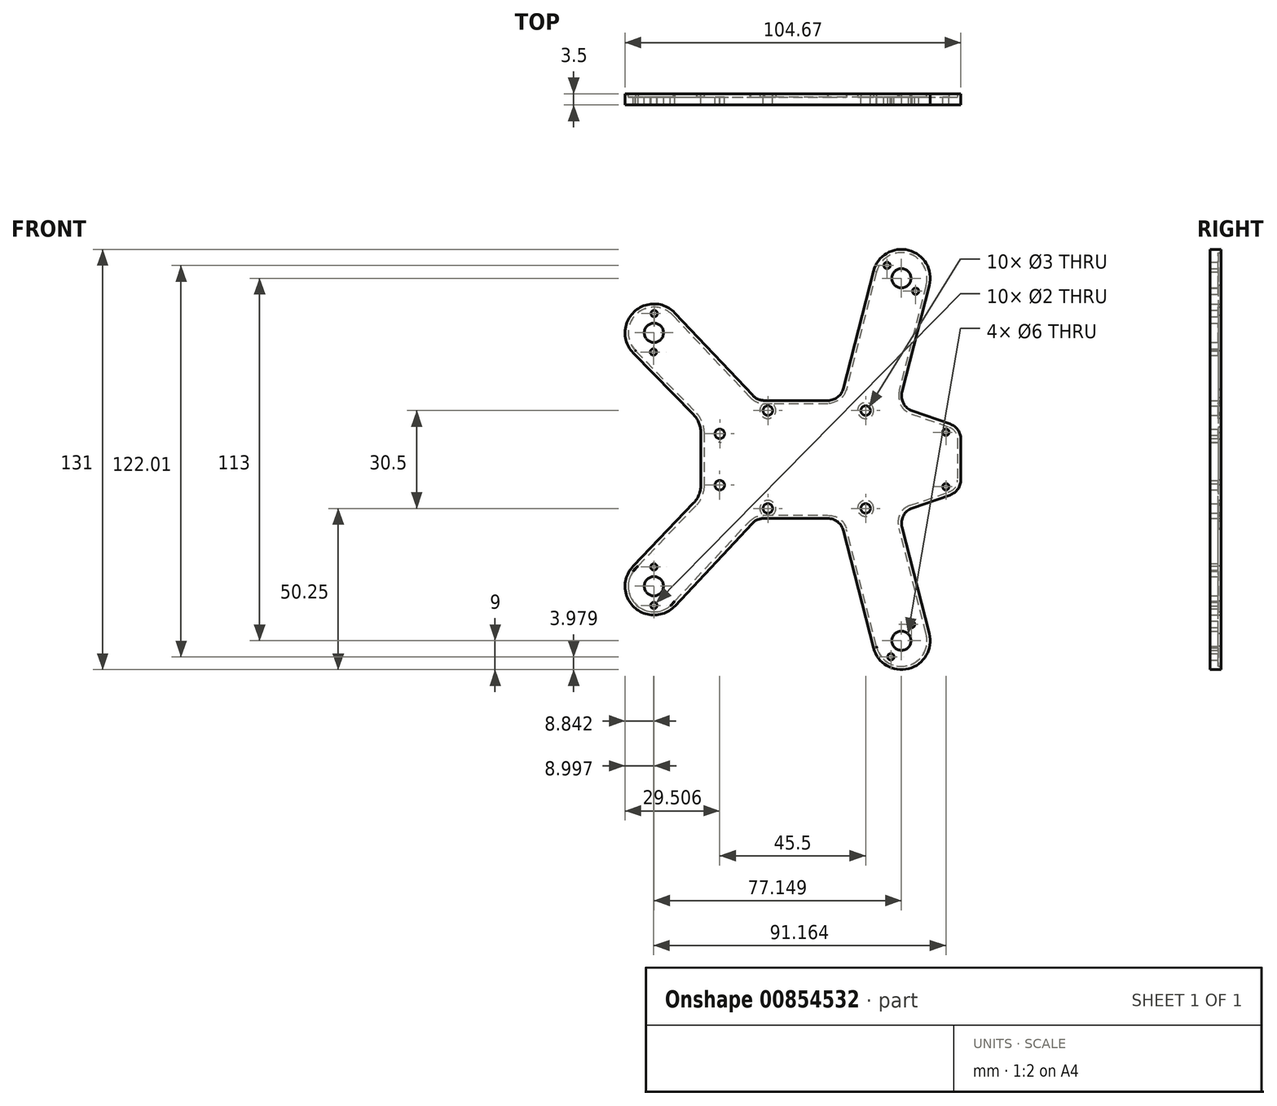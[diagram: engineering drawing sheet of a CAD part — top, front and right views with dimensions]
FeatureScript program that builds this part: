
annotation { "Feature Type Name" : "Feature", "Feature Type Description" : "" }
export const myFeature = defineFeature(function(context is Context, id is Id, definition is map)
    precondition{}
    {
        {
            var Q0;
            Q0=qCreatedBy(makeId("Front.planeOp"),FACE);
            var sketch = newSketch(context, id + "F0", { "sketchPlane" : qUnion([Q0])});
            skLineSegment(sketch, "E0.bottom", {"start": v(-3.88, -18.39) * mm, "end": v(-23.86, -18.39) * mm});
            skLineSegment(sketch, "E0.top", {"start": v(-3.88, 18.39) * mm, "end": v(-23.64, 18.39) * mm});
            skLineSegment(sketch, "E0.left", {"start": v(37.58, -6.33) * mm, "end": v(37.58, -5.89) * mm});
            skLineSegment(sketch, "E0.right", {"start": v(-37.58, -5.3) * mm, "end": v(-37.58, 5.3) * mm});
            skPoint(sketch, "E0.middle", {"position": v(0, 0) * mm});
            skPoint(sketch, "E1", {"position": v(-22.58, 15.25) * mm});
            skPoint(sketch, "E2", {"position": v(-22.58, -15.25) * mm});
            skPoint(sketch, "E3", {"position": v(7.92, 15.25) * mm});
            skPoint(sketch, "E4", {"position": v(7.92, -15.25) * mm});
            skPoint(sketch, "E5", {"position": v(32.92, 8.5) * mm});
            skPoint(sketch, "E6", {"position": v(32.92, -8.5) * mm});
            skCircle(sketch, "E7", {"center": v(-22.58, 15.25) * mm, "radius": 1.5 * mm});
            skCircle(sketch, "E8", {"center": v(-22.58, -15.25) * mm, "radius": 1.5 * mm});
            skCircle(sketch, "E9", {"center": v(7.92, 15.25) * mm, "radius": 1.5 * mm});
            skCircle(sketch, "E10", {"center": v(7.92, -15.25) * mm, "radius": 1.5 * mm});
            skCircle(sketch, "E11", {"center": v(32.92, 8.5) * mm, "radius": 1 * mm});
            skCircle(sketch, "E12", {"center": v(32.92, -8.5) * mm, "radius": 1 * mm});
            skArc(sketch, "E13", {"start": v(-37.47, 5.41) * mm, "mid": v(-37.53, 5.35) * mm, "end": v(-37.58, 5.3) * mm});
            skLineSegment(sketch, "E14", {"start": v(-37.47, 5.41) * mm, "end": v(-37.58, 5.3) * mm});
            skPoint(sketch, "E15.orphan", {"position": v(-37.58, 18.39) * mm});
            skPoint(sketch, "E16.orphan", {"position": v(-37.58, -18.39) * mm});
            skPoint(sketch, "E17", {"position": v(37.58, -9.89) * mm});
            skPoint(sketch, "E18", {"position": v(37.58, 9.89) * mm});
            skLineSegment(sketch, "E19", {"start": v(22.48, 15.14) * mm, "end": v(34.23, 11.05) * mm});
            skLineSegment(sketch, "E20", {"start": v(22.48, -15.14) * mm, "end": v(34.23, -11.05) * mm});
            skPoint(sketch, "E21.orphan", {"position": v(37.58, 18.39) * mm});
            skPoint(sketch, "E22.orphan", {"position": v(37.58, -18.39) * mm});
            skPoint(sketch, "E23", {"position": v(37.58, 5.89) * mm});
            skPoint(sketch, "E24", {"position": v(37.58, -5.89) * mm});
            skLineSegment(sketch, "E25.trimOffspring", {"start": v(37.58, 5.89) * mm, "end": v(37.58, 6.33) * mm});
            skPoint(sketch, "E26", {"position": v(-58.1, 39.5) * mm});
            skPoint(sketch, "E27", {"position": v(-58.1, -39.5) * mm});
            skPoint(sketch, "E28", {"position": v(19.06, -56.5) * mm});
            skPoint(sketch, "E29", {"position": v(19.06, 56.5) * mm});
            skPoint(sketch, "E30.center.orphan", {"position": v(-19.86, 0) * mm});
            skPoint(sketch, "E31.center.orphan", {"position": v(23.9, 0) * mm});
            skLineSegment(sketch, "E32", {"start": v(37.58, 5.89) * mm, "end": v(37.58, -5.89) * mm});
            skCircle(sketch, "E33", {"center": v(-58.1, -39.5) * mm, "radius": 3 * mm});
            skCircle(sketch, "E34", {"center": v(-58.1, 39.5) * mm, "radius": 3 * mm});
            skCircle(sketch, "E35", {"center": v(19.06, 56.5) * mm, "radius": 3 * mm});
            skCircle(sketch, "E36", {"center": v(19.06, -56.5) * mm, "radius": 3 * mm});
            skArc(sketch, "E37", {"start": v(-64.59, -33.27) * mm, "mid": v(-64.28, -46.03) * mm, "end": v(-51.52, -45.65) * mm});
            skArc(sketch, "E38", {"start": v(10.34, -58.73) * mm, "mid": v(21.29, -65.22) * mm, "end": v(27.77, -54.27) * mm});
            skArc(sketch, "E39", {"start": v(-51.55, 45.68) * mm, "mid": v(-64.33, 46) * mm, "end": v(-64.53, 33.21) * mm});
            skArc(sketch, "E40", {"start": v(27.77, 54.27) * mm, "mid": v(21.29, 65.22) * mm, "end": v(10.34, 58.73) * mm});
            skLineSegment(sketch, "E41", {"start": v(-45.75, 13.98) * mm, "end": v(-64.53, 33.21) * mm});
            skLineSegment(sketch, "E42", {"start": v(-27.27, 19.96) * mm, "end": v(-51.55, 45.68) * mm});
            skLineSegment(sketch, "E43", {"start": v(-27.52, -19.97) * mm, "end": v(-51.52, -45.65) * mm});
            skLineSegment(sketch, "E44", {"start": v(-45.7, -13.58) * mm, "end": v(-64.59, -33.27) * mm});
            skLineSegment(sketch, "E45", {"start": v(27.77, 54.27) * mm, "end": v(19.28, 21.1) * mm});
            skLineSegment(sketch, "E46", {"start": v(19.28, -21.1) * mm, "end": v(27.77, -54.27) * mm});
            skLineSegment(sketch, "E47", {"start": v(0.96, -22.15) * mm, "end": v(10.34, -58.73) * mm});
            skLineSegment(sketch, "E48", {"start": v(0.96, 22.15) * mm, "end": v(10.34, 58.73) * mm});
            skLineSegment(sketch, "E49", {"start": v(-43.47, 8.4) * mm, "end": v(-43.47, -8.04) * mm});
            skPoint(sketch, "E50.newPointA", {"position": v(13.14, -18.39) * mm});
            skPoint(sketch, "E50.newPointB", {"position": v(0, -18.39) * mm});
            skArc(sketch, "E50.filletArc", {"start": v(0.96, -22.15) * mm, "mid": v(-0.81, -19.44) * mm, "end": v(-3.88, -18.39) * mm});
            skPoint(sketch, "E51.newPointA", {"position": v(0, 18.39) * mm});
            skPoint(sketch, "E51.newPointB", {"position": v(13.14, 18.39) * mm});
            skArc(sketch, "E51.filletArc", {"start": v(-3.88, 18.39) * mm, "mid": v(-0.81, 19.44) * mm, "end": v(0.96, 22.15) * mm});
            skPoint(sketch, "E52.visualSharp", {"position": v(-25.8, 18.39) * mm});
            skArc(sketch, "E52.filletArc", {"start": v(-27.27, 19.96) * mm, "mid": v(-25.62, 18.8) * mm, "end": v(-23.64, 18.39) * mm});
            skPoint(sketch, "E53.visualSharp", {"position": v(-26.03, -18.39) * mm});
            skArc(sketch, "E53.filletArc", {"start": v(-23.86, -18.39) * mm, "mid": v(-25.85, -18.8) * mm, "end": v(-27.52, -19.97) * mm});
            skArc(sketch, "E54.filletArc", {"start": v(-45.7, -13.58) * mm, "mid": v(-44.05, -11.02) * mm, "end": v(-43.47, -8.04) * mm});
            skArc(sketch, "E55.filletArc", {"start": v(-43.47, 8.4) * mm, "mid": v(-44.06, 11.41) * mm, "end": v(-45.75, 13.98) * mm});
            skPoint(sketch, "E56.newPointA", {"position": v(18.14, 16.65) * mm});
            skArc(sketch, "E56.filletArc", {"start": v(19.28, 21.1) * mm, "mid": v(19.72, 17.5) * mm, "end": v(22.48, 15.14) * mm});
            skPoint(sketch, "E57.newPointB", {"position": v(18.14, -16.65) * mm});
            skArc(sketch, "E57.filletArc", {"start": v(22.48, -15.14) * mm, "mid": v(19.72, -17.5) * mm, "end": v(19.28, -21.1) * mm});
            skArc(sketch, "E58.filletArc", {"start": v(34.23, -11.05) * mm, "mid": v(36.66, -9.23) * mm, "end": v(37.58, -6.33) * mm});
            skArc(sketch, "E59.filletArc", {"start": v(37.58, 6.33) * mm, "mid": v(36.66, 9.23) * mm, "end": v(34.23, 11.05) * mm});
            skLineSegment(sketch, "E60", {"start": v(-37.56, 8) * mm, "end": v(-37.56, 0) * mm});
            skLineSegment(sketch, "E61", {"start": v(-37.56, 0) * mm, "end": v(-37.58, -8) * mm});
            skCircle(sketch, "E62", {"center": v(-37.56, 8) * mm, "radius": 1.5 * mm});
            skCircle(sketch, "E63", {"center": v(-37.58, -8) * mm, "radius": 1.5 * mm});
            skCircle(sketch, "E64", {"center": v(-58.02, 45.5) * mm, "radius": 1 * mm});
            skCircle(sketch, "E65", {"center": v(-58.25, 33.5) * mm, "radius": 1 * mm});
            skCircle(sketch, "E66", {"center": v(-58.1, -33.5) * mm, "radius": 1 * mm});
            skCircle(sketch, "E67", {"center": v(-58.1, -45.5) * mm, "radius": 1 * mm});
            skCircle(sketch, "E68", {"center": v(14.57, 60.49) * mm, "radius": 1 * mm});
            skCircle(sketch, "E69", {"center": v(23.49, 52.46) * mm, "radius": 1 * mm});
            skCircle(sketch, "E70", {"center": v(15.77, -61.52) * mm, "radius": 1 * mm});
            skCircle(sketch, "E71", {"center": v(22.24, -51.42) * mm, "radius": 1 * mm});
            skArc(sketch, "E72", {"start": v(-63.03, -33.2) * mm, "mid": v(-63.64, -45.26) * mm, "end": v(-51.62, -44.2) * mm});
            skLineSegment(sketch, "E73", {"start": v(-64.59, -34.83) * mm, "end": v(-44.8, -14.2) * mm});
            skLineSegment(sketch, "E74", {"start": v(-52.97, -45.65) * mm, "end": v(-28.27, -19.22) * mm});
            skLineSegment(sketch, "E75", {"start": v(-23.86, -17.39) * mm, "end": v(-3.93, -17.39) * mm});
            skArc(sketch, "E76", {"start": v(11.25, -58.24) * mm, "mid": v(21.04, -64.25) * mm, "end": v(26.74, -54.27) * mm});
            skLineSegment(sketch, "E77", {"start": v(11.37, -58.73) * mm, "end": v(1.9, -21.79) * mm});
            skLineSegment(sketch, "E78", {"start": v(26.74, -54.27) * mm, "end": v(18.34, -21.5) * mm});
            skLineSegment(sketch, "E79", {"start": v(21.69, -14.35) * mm, "end": v(33.57, -10.22) * mm});
            skLineSegment(sketch, "E80", {"start": v(36.58, 6.32) * mm, "end": v(36.58, -6.4) * mm});
            skLineSegment(sketch, "E81", {"start": v(22.13, 14.2) * mm, "end": v(33.89, 10.11) * mm});
            skArc(sketch, "E82", {"start": v(26.74, 54.27) * mm, "mid": v(21.14, 64.22) * mm, "end": v(11.3, 58.44) * mm});
            skLineSegment(sketch, "E83", {"start": v(26.74, 54.27) * mm, "end": v(18.38, 21.64) * mm});
            skLineSegment(sketch, "E84", {"start": v(11.32, 58.53) * mm, "end": v(1.93, 21.88) * mm});
            skLineSegment(sketch, "E85", {"start": v(-3.8, 17.39) * mm, "end": v(-23.64, 17.39) * mm});
            skArc(sketch, "E86", {"start": v(-52.15, 44.86) * mm, "mid": v(-63.6, 45.3) * mm, "end": v(-63.75, 33.84) * mm});
            skLineSegment(sketch, "E87", {"start": v(-52.15, 44.86) * mm, "end": v(-28.01, 19.28) * mm});
            skLineSegment(sketch, "E88", {"start": v(-63.88, 33.98) * mm, "end": v(-44.93, 14.58) * mm});
            skLineSegment(sketch, "E89", {"start": v(-42.47, 8.37) * mm, "end": v(-42.47, -7.92) * mm});
            skFitSpline(sketch, "E90", {"points": [v(-44.93, 14.58) * mm, v(-43.18, 11.84) * mm, v(-42.47, 8.37) * mm], "startDerivative": vector(4.86, -5.6) * mm, "endDerivative": vector(0.46, -7.23) * mm});
            skFitSpline(sketch, "E91", {"points": [v(-42.47, -7.92) * mm, v(-43.12, -11.34) * mm, v(-44.8, -14.2) * mm], "startDerivative": vector(0.22, -7.29) * mm, "endDerivative": vector(-5.1, -4.66) * mm});
            skFitSpline(sketch, "E92", {"points": [v(-28.27, -19.22) * mm, v(-26.29, -17.87) * mm, v(-23.86, -17.39) * mm], "startDerivative": vector(3.8, 3.17) * mm, "endDerivative": vector(5.02, 0.51) * mm});
            skFitSpline(sketch, "E93", {"points": [v(-3.93, -17.39) * mm, v(0, -18.61) * mm, v(1.9, -21.79) * mm], "startDerivative": vector(10.59, -0.73) * mm, "endDerivative": vector(2.12, -8.88) * mm});
            skFitSpline(sketch, "E94", {"points": [v(21.69, -14.35) * mm, v(18.53, -17.14) * mm, v(18.34, -21.5) * mm], "startDerivative": vector(-11.12, -4.4) * mm, "endDerivative": vector(3.23, -10.04) * mm});
            skFitSpline(sketch, "E95", {"points": [v(33.57, -10.22) * mm, v(35.81, -8.75) * mm, v(36.58, -6.4) * mm], "startDerivative": vector(5.6, 2) * mm, "endDerivative": vector(0.38, 5.68) * mm});
            skFitSpline(sketch, "E96", {"points": [v(33.89, 10.11) * mm, v(35.88, 8.57) * mm, v(36.58, 6.32) * mm], "startDerivative": vector(5.12, -1.96) * mm, "endDerivative": vector(0.3, -5.6) * mm});
            skFitSpline(sketch, "E97", {"points": [v(18.38, 21.64) * mm, v(18.78, 17.14) * mm, v(22.13, 14.2) * mm], "startDerivative": vector(-1.49, -10.31) * mm, "endDerivative": vector(10.39, -4.84) * mm});
            skFitSpline(sketch, "E98", {"points": [v(1.93, 21.88) * mm, v(0, 18.87) * mm, v(-3.8, 17.39) * mm], "startDerivative": vector(-2.83, -8.6) * mm, "endDerivative": vector(-8.85, -1.05) * mm});
            skFitSpline(sketch, "E99", {"points": [v(-28.01, 19.28) * mm, v(-26.03, 17.93) * mm, v(-23.64, 17.39) * mm], "startDerivative": vector(3.44, -3.74) * mm, "endDerivative": vector(5.3, -0.05) * mm});
            skSolve(sketch);
        }
        {
            var Q0;
            Q0=makeQuery(id+"F0.imprint","IMPRINT",FACE,{"disambiguationData":[TD([[makeQuery(id+"F0.imprint","IMPRINT",EDGE,{"derivedFrom":sQuery(id+"F0.wireOp",EDGE,"E7")}),-1.0]])]});
            var Q1;
            Q1=makeQuery(id+"F0.imprint","IMPRINT",FACE,{"disambiguationData":[TD([[makeQuery(id+"F0.imprint","IMPRINT",EDGE,{"derivedFrom":sQuery(id+"F0.wireOp",EDGE,"E0.bottom")}),-1.0]])]});
            extrude(context, id + "F1", {"entities" : qUnion([Q0, Q1]), "depth" : 2.5 * mm, "offsetDistance" : 25 * mm});
        }
        {
            var Q0;
            Q0=makeQuery(id+"F0.imprint","IMPRINT",FACE,{"disambiguationData":[TD([[makeQuery(id+"F0.imprint","IMPRINT",EDGE,{"derivedFrom":sQuery(id+"F0.wireOp",EDGE,"E0.bottom")}),-1.0]])]});
            extrude(context, id + "F2", {"entities" : qUnion([Q0]), "operationType" : NewBodyOperationType.ADD, "oppositeDirection" : true, "depth" : 1 * mm, "offsetDistance" : 25 * mm});
        }
        {
            var Q0;
            Q0=makeQuery(id+"F0.imprint","IMPRINT",FACE,{"disambiguationData":[TD([[makeQuery(id+"F0.imprint","IMPRINT",EDGE,{"derivedFrom":sQuery(id+"F0.wireOp",EDGE,"E7")}),-1.0]])]});
            var sketch = newSketch(context, id + "F3", { "sketchPlane" : qUnion([Q0])});
            skCircle(sketch, "E100", {"center": v(-22.58, -15.25) * mm, "radius": 2.5 * mm});
            skCircle(sketch, "E101", {"center": v(7.92, -15.25) * mm, "radius": 2.5 * mm});
            skCircle(sketch, "E102", {"center": v(7.92, 15.25) * mm, "radius": 2.5 * mm});
            skCircle(sketch, "E103", {"center": v(-22.58, 15.25) * mm, "radius": 2.5 * mm});
            skSolve(sketch);
        }
        {
            var Q0;
            Q0=makeQuery(id+"F3.imprint","IMPRINT",FACE,{"disambiguationData":[TD([[makeQuery(id+"F3.imprint","IMPRINT",EDGE,{"derivedFrom":makeQuery(id+"F0.imprint","IMPRINT",EDGE,{"derivedFrom":sQuery(id+"F0.wireOp",EDGE,"E8")})}),-1.0]])]});
            var Q1;
            Q1=makeQuery(id+"F3.imprint","IMPRINT",FACE,{"disambiguationData":[TD([[makeQuery(id+"F3.imprint","IMPRINT",EDGE,{"derivedFrom":sQuery(id+"F3.wireOp",EDGE,"E101")}),1.0]])]});
            var Q2;
            Q2=makeQuery(id+"F3.imprint","IMPRINT",FACE,{"disambiguationData":[TD([[makeQuery(id+"F3.imprint","IMPRINT",EDGE,{"derivedFrom":sQuery(id+"F3.wireOp",EDGE,"E102")}),1.0]])]});
            var Q3;
            Q3=makeQuery(id+"F3.imprint","IMPRINT",FACE,{"disambiguationData":[TD([[makeQuery(id+"F3.imprint","IMPRINT",EDGE,{"derivedFrom":makeQuery(id+"F0.imprint","IMPRINT",EDGE,{"derivedFrom":sQuery(id+"F0.wireOp",EDGE,"E7")})}),-1.0]])]});
            extrude(context, id + "F4", {"entities" : qUnion([Q0, Q1, Q2, Q3]), "oppositeDirection" : true, "depth" : 1 * mm, "offsetDistance" : 25 * mm});
        }
    });
